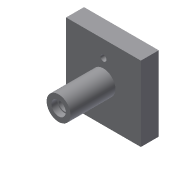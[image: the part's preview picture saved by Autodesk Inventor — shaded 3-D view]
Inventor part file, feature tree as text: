
AUTODESK INVENTOR PART (.ipt)
format: ipt  version: 2017 (Build 210142000, 142)  size: 106,496 bytes
history: native  units: in
note: dims shown in document units (in); Inventor stores cm internally (conversion verified against a paired STEP export)
features: sketch x3, extrude x2, hole x2, plane x1, pattern_circular x1
ambient origin geometry x8: Origin, YZ Plane, XZ Plane, XY Plane, X Axis, Y Axis, Z Axis, Center Point
bodies: Solid1 (feature_tree)
feature tree (9):
  plane  "Work Plane1"
  extrude  "Extrusion1"  Depth=6.25in
  extrude  "Extrusion2"  Depth=1.5in
  hole  "Hole1"  [1 undecoded]
  hole  "Hole2"  [1 undecoded]
  pattern_circular  "Circular Pattern1"  Count=4 Angle=360.0deg
  sketch  "Sketch1"  dims[d0=6.25in d1=6.25in]
  sketch  "Sketch2"  dims[d2=1.5in d3=0.0in d4=2.0in]
  sketch  "Sketch3"  dims[d5=3.75in d6=0.0in d7=1.0in d8=1.0in d9=1.0in d10=0.75in d11=1.2in d12=0.5in d13=0.5635in d14=1.0in d15=0.8108in d16=3.5in d17=0.5in d18=0.75in d19=1.2in d20=0.5in d21=0.5635in d22=1.0in d23=0.8108in d24=1.5748in d25=360.0deg]
note: 2 required parameter values undecoded (feature->parameter linkage not recoverable at this tier; creation-order binding heuristic only, values carry confidence <= 0.55)
